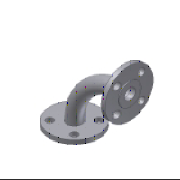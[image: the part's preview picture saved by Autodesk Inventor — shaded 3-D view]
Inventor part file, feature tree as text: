
AUTODESK INVENTOR PART (.ipt)
format: ipt  version: 2023.2 (Build 272271030, 271C)  size: 310,784 bytes
history: native  units: mm (DEFAULTED — no unit token found)
features: sketch x5, other x4, revolve x2, extrude x2, pattern_circular x2, sweep x1
ambient origin geometry x8: Origin, YZ Plane, XZ Plane, XY Plane, X Axis, Y Axis, Z Axis, Center Point
bodies: Solid1 (feature_tree)
feature tree (16):
  sketch  "Sketch1"  dims[d0=387.0mm d1=600.0mm]
  revolve  "Revolution1"  [1 undecoded]
  revolve  "Revolution2"  [1 undecoded]
  sweep  "Sweep1"
  extrude  "Extrusion1"  Depth=37.0mm
  pattern_circular  "Circular Pattern1"  Count=47  [1 undecoded]
  extrude  "Extrusion2"  Depth=600.0mm
  pattern_circular  "Circular Pattern2"  Count=61  [1 undecoded]
  other  "Work Point1"
  other  "Work Point2"
  other  "Work Axis1"
  other  "Work Axis2"
  sketch  "Sketch2"  dims[d2=470.0mm d3=2.0mm]
  sketch  "Sketch3"  dims[d4=37.0mm d5=90.0deg]
  sketch  "Sketch6"  dims[d6=2.0mm d7=37.0mm]
  sketch  "Sketch7"  dims[d8=387.0mm d9=470.0mm d10=600.0mm d11=610.0mm d12=610.0mm d13=90.0deg d14=409.2mm d15=0.0mm d16=160.0mm d17=360.0deg d18=160.0mm d19=360.0deg d20=1.963495mm d21=29.5mm d22=540.0mm d34=25.4mm d24=0.0mm d25=1.963495mm d26=29.5mm d27=540.0mm d39=25.4mm d28=0.0mm d41=0.0mm]
note: 4 required parameter values undecoded (feature->parameter linkage not recoverable at this tier; creation-order binding heuristic only, values carry confidence <= 0.55)